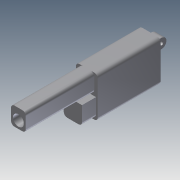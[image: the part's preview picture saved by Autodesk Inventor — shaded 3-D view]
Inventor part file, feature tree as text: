
AUTODESK INVENTOR PART (.ipt)
format: ipt  version: 2011 (Build 150239000, 239)  size: 219,136 bytes
history: native  units: in
note: dims shown in document units (in); Inventor stores cm internally (conversion verified against a paired STEP export)
features: extrude x13, sketch x13, fillet x1
ambient origin geometry x8: Origin, YZ Plane, XZ Plane, XY Plane, X Axis, Y Axis, Z Axis, Center Point
bodies: Solid1 (feature_tree)
feature tree (27):
  extrude  "Extrusion1"  Depth=2.91in
  extrude  "Extrusion2"  Depth=1.56in
  extrude  "Extrusion3"  Depth=0.25in
  extrude  "Extrusion4"  Depth=6.4in TaperAngle=0.0deg
  extrude  "Extrusion5"  Depth=8.0in TaperAngle=0.0deg
  extrude  "Extrusion6"  Depth=1.31in
  extrude  "Extrusion7"  Depth=1.0in TaperAngle=0.0deg
  extrude  "Extrusion8"  Depth=0.7in
  extrude  "Extrusion9"  Depth=0.25in
  extrude  "Extrusion10"  Depth=0.7in TaperAngle=0.0deg
  fillet  "Fillet1"  Radius=1.5in
  extrude  "Extrusion11"  Depth=0.78in
  extrude  "Extrusion12"  Depth=9.0in TaperAngle=0.0deg
  extrude  "Extrusion13"  [1 undecoded]
  sketch  "Sketch1"  dims[d0=1.56in d1=2.91in]
  sketch  "Sketch2"  dims[d2=3.0in d3=0.0in d4=1.56in]
  sketch  "Sketch3"  dims[d5=0.25in d6=0.25in]
  sketch  "Sketch4"  dims[d7=1.06in d8=6.4in d9=0.0in]
  sketch  "Sketch5"  dims[d10=0.78in d11=8.0in d12=0.0in]
  sketch  "Sketch6"  dims[d13=1.0in d14=0.0in d15=1.31in]
  sketch  "Sketch7"  dims[d16=3.5in d17=0.0in d18=1.0in d19=0.0in]
  sketch  "Sketch8"  dims[d20=45.0deg d21=0.7in]
  sketch  "Sketch9"  dims[d22=0.5in d23=0.0in d24=0.25in]
  sketch  "Sketch10"  dims[d25=1.0in d26=0.0in d27=0.7in d28=0.0in d29=1.5in d30=0.0in]
  sketch  "Sketch11"  dims[d31=0.25in d32=0.78in]
  sketch  "Sketch12"  dims[d33=4.0in d34=0.0in d35=9.0in d36=0.0in]
  sketch  "Sketch13"  dims[d37=4.0in d38=0.0in]
note: 1 required parameter value undecoded (feature->parameter linkage not recoverable at this tier; creation-order binding heuristic only, values carry confidence <= 0.55)
